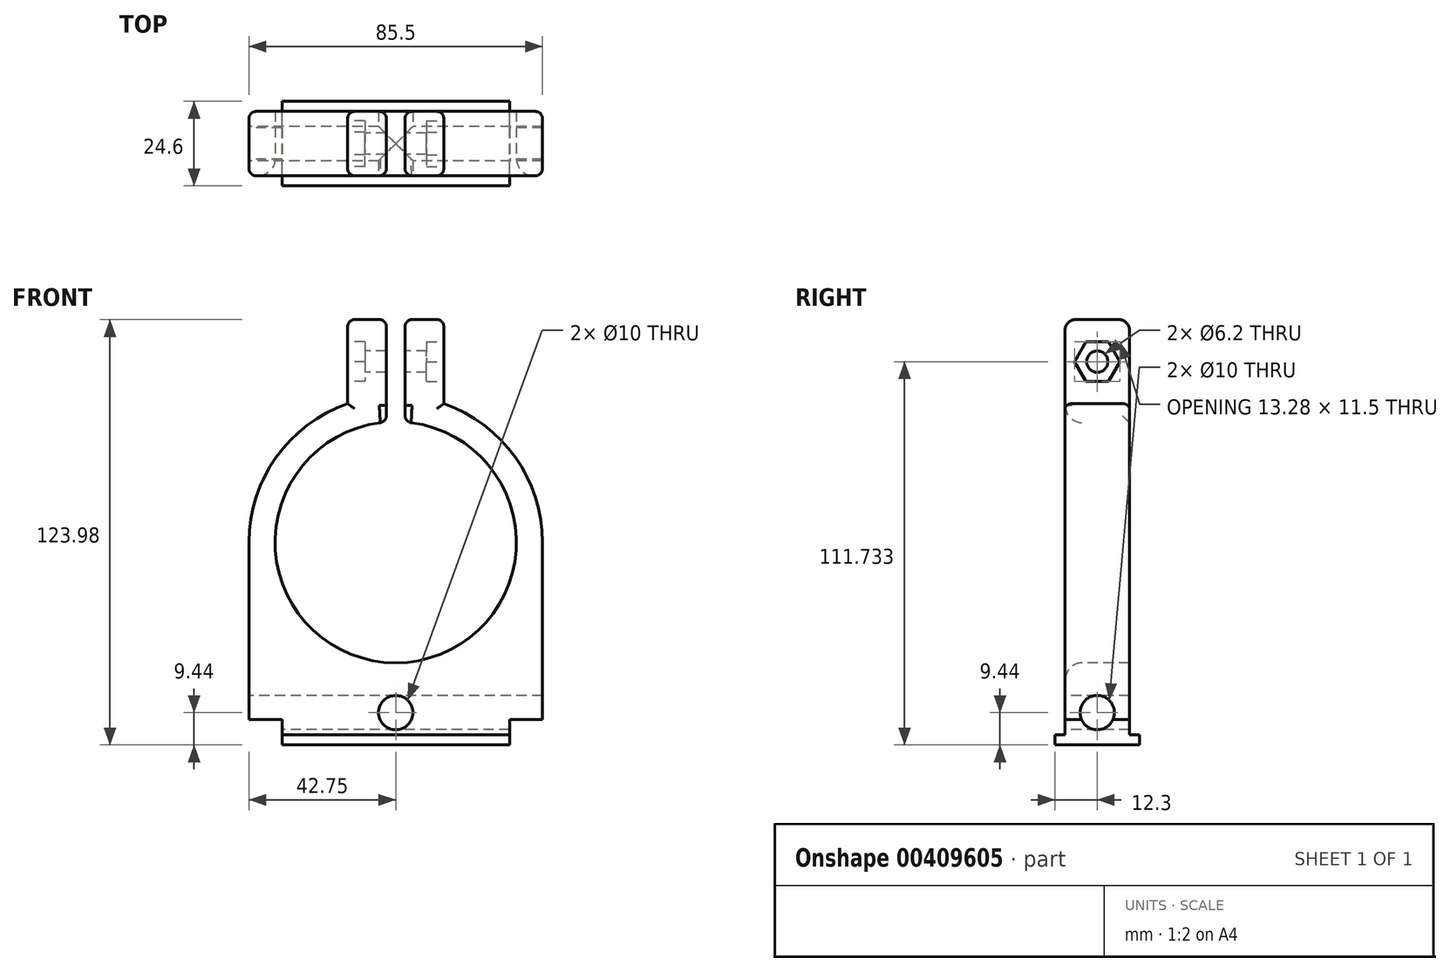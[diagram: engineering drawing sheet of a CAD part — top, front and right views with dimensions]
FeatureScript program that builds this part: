
annotation { "Feature Type Name" : "Feature", "Feature Type Description" : "" }
export const myFeature = defineFeature(function(context is Context, id is Id, definition is map)
    precondition{}
    {
        {
            var Q0;
            Q0=qCreatedBy(makeId("Top.planeOp"),FACE);
            var sketch = newSketch(context, id + "F0", { "sketchPlane" : qUnion([Q0])});
            skLineSegment(sketch, "E0.bottom", {"start": v(33.15, -12.3) * mm, "end": v(-33.15, -12.3) * mm});
            skLineSegment(sketch, "E0.top", {"start": v(33.15, 12.3) * mm, "end": v(-33.15, 12.3) * mm});
            skLineSegment(sketch, "E0.left", {"start": v(33.15, -12.3) * mm, "end": v(33.15, 12.3) * mm});
            skLineSegment(sketch, "E0.right", {"start": v(-33.15, -12.3) * mm, "end": v(-33.15, 12.3) * mm});
            skPoint(sketch, "E0.middle", {"position": v(0, 0) * mm});
            skSolve(sketch);
        }
        {
            var Q0;
            Q0 = qSketchRegion(id + "F0", true);
            extrude(context, id + "F1", {"entities" : qUnion([Q0]), "depth" : 2.94 * mm});
        }
        {
            var Q0;
            Q0=makeQuery(id+"F1.opExtrude","CAP_FACE",FACE,{"disambiguationData":[OSD([sQuery(id+"F0.wireOp",EDGE,"E0.bottom"),sQuery(id+"F0.wireOp",EDGE,"E0.top"),sQuery(id+"F0.wireOp",EDGE,"E0.left"),sQuery(id+"F0.wireOp",EDGE,"E0.right")])],"isStart":false});
            var sketch = newSketch(context, id + "F2", { "sketchPlane" : qUnion([Q0])});
            skLineSegment(sketch, "E1.bottom", {"start": v(33.15, -9.38) * mm, "end": v(-33.15, -9.38) * mm});
            skLineSegment(sketch, "E1.top", {"start": v(33.15, 9.38) * mm, "end": v(-33.15, 9.38) * mm});
            skLineSegment(sketch, "E1.left", {"start": v(33.15, -9.38) * mm, "end": v(33.15, 9.38) * mm});
            skLineSegment(sketch, "E1.right", {"start": v(-33.15, -9.38) * mm, "end": v(-33.15, 9.38) * mm});
            skPoint(sketch, "E1.middle", {"position": v(0, 0) * mm});
            skSolve(sketch);
        }
        {
            var Q0;
            Q0 = qSketchRegion(id + "F2", true);
            extrude(context, id + "F3", {"entities" : qUnion([Q0]), "operationType" : NewBodyOperationType.ADD, "depth" : 4.5 * mm});
        }
        {
            var Q0;
            Q0=makeQuery(id+"F3.opExtrude","SWEPT_FACE",FACE,{"disambiguationData":[OSD([sQuery(id+"F2.wireOp",EDGE,"E1.bottom")])]});
            var sketch = newSketch(context, id + "F4", { "sketchPlane" : qUnion([Q0])});
            skArc(sketch, "E2", {"start": v(-2.75, 94.13) * mm, "mid": v(0, 23.94) * mm, "end": v(2.75, 94.13) * mm});
            skArc(sketch, "E3.0", {"start": v(42.75, 59.1) * mm, "mid": v(34.83, 83.88) * mm, "end": v(14, 99.48) * mm});
            skLineSegment(sketch, "E4", {"start": v(-42.75, 59.1) * mm, "end": v(-42.75, 7.44) * mm});
            skLineSegment(sketch, "E5", {"start": v(42.75, 59.1) * mm, "end": v(42.75, 7.44) * mm});
            skLineSegment(sketch, "E6", {"start": v(42.75, 7.44) * mm, "end": v(-42.75, 7.44) * mm});
            skLineSegment(sketch, "E7.top", {"start": v(14, 123.98) * mm, "end": v(2.75, 123.98) * mm});
            skLineSegment(sketch, "E7.left", {"start": v(14, 99.48) * mm, "end": v(14, 123.98) * mm});
            skLineSegment(sketch, "E7.right", {"start": v(-14, 99.48) * mm, "end": v(-14, 123.98) * mm});
            skPoint(sketch, "E7.middle", {"position": v(0, 111.73) * mm});
            skArc(sketch, "E8.trimOffspring", {"start": v(-14, 99.48) * mm, "mid": v(-34.83, 83.88) * mm, "end": v(-42.75, 59.1) * mm});
            skLineSegment(sketch, "E9", {"start": v(-2.75, 94.13) * mm, "end": v(-2.75, 123.98) * mm});
            skLineSegment(sketch, "E10", {"start": v(2.75, 94.13) * mm, "end": v(2.75, 123.98) * mm});
            skLineSegment(sketch, "E11.trimOffspring", {"start": v(-2.75, 123.98) * mm, "end": v(-14, 123.98) * mm});
            skLineSegment(sketch, "E12", {"start": v(-2.75, 123.98) * mm, "end": v(2.75, 123.98) * mm, "construction": true});
            skLineSegment(sketch, "E13", {"start": v(0, 123.98) * mm, "end": v(0, 111.73) * mm, "construction": true});
            skSolve(sketch);
        }
        {
            var Q0;
            Q0 = qSketchRegion(id + "F4", true);
            var Q1;
            Q1=makeQuery(id+"F3.opExtrude","SWEPT_FACE",FACE,{"disambiguationData":[OSD([sQuery(id+"F2.wireOp",EDGE,"E1.top")])]});
            extrude(context, id + "F5", {"entities" : qUnion([Q0]), "operationType" : NewBodyOperationType.ADD, "endBound" : BoundingType.UP_TO_SURFACE, "oppositeDirection" : true, "endBoundEntityFace" : qUnion([Q1]), "depth" : 25 * mm});
        }
        {
            var Q0;
            Q0=makeQuery(id+"F5.opExtrude","SWEPT_FACE",FACE,{"disambiguationData":[OSD([sQuery(id+"F4.wireOp",EDGE,"E7.right")])]});
            var sketch = newSketch(context, id + "F6", { "sketchPlane" : qUnion([Q0])});
            skCircle(sketch, "E14.cCircle", {"center": v(0, 111.73) * mm, "radius": 5.75 * mm, "construction": true});
            skPoint(sketch, "E14.cCircle.centerSnap0", {"position": v(9.38, 111.73) * mm});
            skLineSegment(sketch, "E14.0", {"start": v(3.32, 105.98) * mm, "end": v(-3.32, 105.98) * mm});
            skLineSegment(sketch, "E14.1", {"start": v(-3.32, 105.98) * mm, "end": v(-6.64, 111.73) * mm});
            skLineSegment(sketch, "E14.2", {"start": v(-6.64, 111.73) * mm, "end": v(-3.32, 117.48) * mm});
            skLineSegment(sketch, "E14.3", {"start": v(-3.32, 117.48) * mm, "end": v(3.32, 117.48) * mm});
            skLineSegment(sketch, "E14.4", {"start": v(3.32, 117.48) * mm, "end": v(6.64, 111.73) * mm});
            skLineSegment(sketch, "E14.5", {"start": v(6.64, 111.73) * mm, "end": v(3.32, 105.98) * mm});
            skPoint(sketch, "E14.0.midPoint", {"position": v(0, 105.98) * mm});
            skSolve(sketch);
        }
        {
            var Q0;
            Q0 = qSketchRegion(id + "F6", true);
            extrude(context, id + "F7", {"entities" : qUnion([Q0]), "operationType" : NewBodyOperationType.REMOVE, "oppositeDirection" : true, "depth" : 5 * mm});
        }
        {
            var Q0;
            Q0=makeQuery(id+"F5.opExtrude","SWEPT_FACE",FACE,{"disambiguationData":[OSD([sQuery(id+"F4.wireOp",EDGE,"E7.left")])]});
            var sketch = newSketch(context, id + "F8", { "sketchPlane" : qUnion([Q0])});
            skLineSegment(sketch, "E15.0.0", {"start": v(-3.32, 105.98) * mm, "end": v(-6.64, 111.73) * mm});
            skLineSegment(sketch, "E15.0.1", {"start": v(-6.64, 111.73) * mm, "end": v(-3.32, 117.48) * mm});
            skLineSegment(sketch, "E15.0.2", {"start": v(-3.32, 117.48) * mm, "end": v(3.32, 117.48) * mm});
            skLineSegment(sketch, "E15.0.3", {"start": v(3.32, 117.48) * mm, "end": v(6.64, 111.73) * mm});
            skLineSegment(sketch, "E15.0.4", {"start": v(6.64, 111.73) * mm, "end": v(3.32, 105.98) * mm});
            skLineSegment(sketch, "E15.0.5", {"start": v(3.32, 105.98) * mm, "end": v(-3.32, 105.98) * mm});
            skSolve(sketch);
        }
        {
            var Q0;
            Q0 = qSketchRegion(id + "F8", true);
            extrude(context, id + "F9", {"entities" : qUnion([Q0]), "operationType" : NewBodyOperationType.REMOVE, "oppositeDirection" : true, "depth" : 5 * mm});
        }
        {
            var Q0;
            Q0=makeQuery(id+"F7.boolean.opBoolean","COPY",FACE,{"derivedFrom":makeQuery(id+"F7.opExtrude","CAP_FACE",FACE,{"disambiguationData":[OSD([sQuery(id+"F6.wireOp",EDGE,"E14.0"),sQuery(id+"F6.wireOp",EDGE,"E14.1"),sQuery(id+"F6.wireOp",EDGE,"E14.2"),sQuery(id+"F6.wireOp",EDGE,"E14.3"),sQuery(id+"F6.wireOp",EDGE,"E14.4"),sQuery(id+"F6.wireOp",EDGE,"E14.5")])],"isStart":false})});
            var sketch = newSketch(context, id + "F10", { "sketchPlane" : qUnion([Q0])});
            skCircle(sketch, "E16", {"center": v(0, 111.73) * mm, "radius": 3.1 * mm});
            skPoint(sketch, "E16.centerSnap0", {"position": v(0, 117.48) * mm});
            skSolve(sketch);
        }
        {
            var Q0;
            Q0 = qSketchRegion(id + "F10", true);
            extrude(context, id + "F11", {"entities" : qUnion([Q0]), "operationType" : NewBodyOperationType.REMOVE, "endBound" : BoundingType.THROUGH_ALL, "oppositeDirection" : true, "depth" : 25 * mm});
        }
        {
            var Q0;
            Q0=makeQuery(id+"F5.boolean.opBoolean","MERGE",FACE,{"derivedFrom":[makeQuery(id+"F3.opExtrude","SWEPT_FACE",FACE,{"disambiguationData":[OSD([sQuery(id+"F2.wireOp",EDGE,"E1.bottom")])]}),makeQuery(id+"F5.opExtrude","CAP_FACE",FACE,{"disambiguationData":[OSD([sQuery(id+"F4.wireOp",EDGE,"E2"),sQuery(id+"F4.wireOp",EDGE,"E3.0"),sQuery(id+"F4.wireOp",EDGE,"E4"),sQuery(id+"F4.wireOp",EDGE,"E5"),sQuery(id+"F4.wireOp",EDGE,"E6"),sQuery(id+"F4.wireOp",EDGE,"E7.top"),sQuery(id+"F4.wireOp",EDGE,"E7.left"),sQuery(id+"F4.wireOp",EDGE,"E7.right"),sQuery(id+"F4.wireOp",EDGE,"E8.trimOffspring"),sQuery(id+"F4.wireOp",EDGE,"E9"),sQuery(id+"F4.wireOp",EDGE,"E10"),sQuery(id+"F4.wireOp",EDGE,"E11.trimOffspring")])],"isStart":true})]});
            var sketch = newSketch(context, id + "F12", { "sketchPlane" : qUnion([Q0])});
            skCircle(sketch, "E17", {"center": v(0, 9.44) * mm, "radius": 5 * mm});
            skPoint(sketch, "E17.centerSnap0", {"position": v(0, 2.94) * mm});
            skSolve(sketch);
        }
        {
            var Q0;
            Q0 = qSketchRegion(id + "F12", true);
            extrude(context, id + "F13", {"entities" : qUnion([Q0]), "operationType" : NewBodyOperationType.REMOVE, "endBound" : BoundingType.THROUGH_ALL, "oppositeDirection" : true, "depth" : 25 * mm});
        }
        {
            var Q0;
            Q0=makeQuery(id+"F5.opExtrude","SWEPT_FACE",FACE,{"disambiguationData":[OSD([sQuery(id+"F4.wireOp",EDGE,"E4")])]});
            var sketch = newSketch(context, id + "F14", { "sketchPlane" : qUnion([Q0])});
            skCircle(sketch, "E18", {"center": v(0, 9.44) * mm, "radius": 5 * mm});
            skPoint(sketch, "E18.centerSnap0", {"position": v(0, 7.44) * mm});
            skLineSegment(sketch, "E19.0", {"start": v(12.3, 2.94) * mm, "end": v(9.38, 2.94) * mm, "construction": true});
            skSolve(sketch);
        }
        {
            var Q0;
            Q0 = qSketchRegion(id + "F14", true);
            extrude(context, id + "F15", {"entities" : qUnion([Q0]), "operationType" : NewBodyOperationType.REMOVE, "endBound" : BoundingType.THROUGH_ALL, "oppositeDirection" : true, "depth" : 25 * mm});
        }
        {
            var Q0;
            Q0=makeQuery(id+"F5.opExtrude","CAP_EDGE",EDGE,{"disambiguationData":[OSD([sQuery(id+"F4.wireOp",EDGE,"E2")])],"isStart":true});
            fillet(context, id + "F16", {"entities" : qUnion([Q0]), "radius" : 5 * mm, "tangentPropagation" : true, "allowEdgeOverflow" : false});
        }
        {
            var Q0;
            Q0=makeQuery(id+"F5.opExtrude","CAP_EDGE",EDGE,{"disambiguationData":[OSD([sQuery(id+"F4.wireOp",EDGE,"E7.top")])],"isStart":true});
            var Q1;
            Q1=makeQuery(id+"F5.opExtrude","CAP_EDGE",EDGE,{"disambiguationData":[OSD([sQuery(id+"F4.wireOp",EDGE,"E11.trimOffspring")])],"isStart":true});
            var Q2;
            Q2=makeQuery(id+"F5.opExtrude","CAP_EDGE",EDGE,{"disambiguationData":[OSD([sQuery(id+"F4.wireOp",EDGE,"E7.top")])],"isStart":false});
            var Q3;
            Q3=makeQuery(id+"F5.opExtrude","CAP_EDGE",EDGE,{"disambiguationData":[OSD([sQuery(id+"F4.wireOp",EDGE,"E11.trimOffspring")])],"isStart":false});
            fillet(context, id + "F17", {"entities" : qUnion([Q0, Q1, Q2, Q3]), "radius" : 3 * mm, "tangentPropagation" : true, "allowEdgeOverflow" : false});
        }
        {
            var Q0;
            Q0=makeQuery(id+"F5.opExtrude","CAP_EDGE",EDGE,{"disambiguationData":[OSD([sQuery(id+"F4.wireOp",EDGE,"E5")])],"isStart":true});
            var Q1;
            Q1=makeQuery(id+"F5.opExtrude","CAP_EDGE",EDGE,{"disambiguationData":[OSD([sQuery(id+"F4.wireOp",EDGE,"E4")])],"isStart":true});
            var Q2;
            Q2=makeQuery(id+"F5.opExtrude","CAP_EDGE",EDGE,{"disambiguationData":[OSD([sQuery(id+"F4.wireOp",EDGE,"E5")])],"isStart":false});
            var Q3;
            Q3=makeQuery(id+"F5.opExtrude","CAP_EDGE",EDGE,{"disambiguationData":[OSD([sQuery(id+"F4.wireOp",EDGE,"E4")])],"isStart":false});
            var Q4;
            Q4=makeQuery(id+"F5.opExtrude","CAP_EDGE",EDGE,{"disambiguationData":[OSD([sQuery(id+"F4.wireOp",EDGE,"E7.left")])],"isStart":true});
            var Q5;
            Q5=makeQuery(id+"F5.opExtrude","CAP_EDGE",EDGE,{"disambiguationData":[OSD([sQuery(id+"F4.wireOp",EDGE,"E7.left")])],"isStart":false});
            var Q6;
            Q6=makeQuery(id+"F5.opExtrude","CAP_EDGE",EDGE,{"disambiguationData":[OSD([sQuery(id+"F4.wireOp",EDGE,"E7.right")])],"isStart":true});
            var Q7;
            Q7=makeQuery(id+"F5.opExtrude","CAP_EDGE",EDGE,{"disambiguationData":[OSD([sQuery(id+"F4.wireOp",EDGE,"E7.right")])],"isStart":false});
            var Q8;
            Q8=makeQuery(id+"F5.opExtrude","SWEPT_EDGE",EDGE,{"disambiguationData":[OSD([sQuery(id+"F4.wireOp",EDGE,"E2"),sQuery(id+"F4.wireOp",EDGE,"E9")])]});
            var Q9;
            Q9=makeQuery(id+"F5.opExtrude","SWEPT_EDGE",EDGE,{"disambiguationData":[OSD([sQuery(id+"F4.wireOp",EDGE,"E2"),sQuery(id+"F4.wireOp",EDGE,"E10")])]});
            var Q10;
            Q10=makeQuery(id+"F5.opExtrude","SWEPT_EDGE",EDGE,{"disambiguationData":[OSD([sQuery(id+"F4.wireOp",EDGE,"E9"),sQuery(id+"F4.wireOp",EDGE,"E11.trimOffspring")])]});
            var Q11;
            Q11=makeQuery(id+"F5.opExtrude","SWEPT_EDGE",EDGE,{"disambiguationData":[OSD([sQuery(id+"F4.wireOp",EDGE,"E7.top"),sQuery(id+"F4.wireOp",EDGE,"E10")])]});
            fillet(context, id + "F18", {"entities" : qUnion([Q0, Q1, Q2, Q3, Q4, Q5, Q6, Q7, Q8, Q9, Q10, Q11]), "radius" : 2 * mm, "tangentPropagation" : true, "allowEdgeOverflow" : false});
        }
    });
